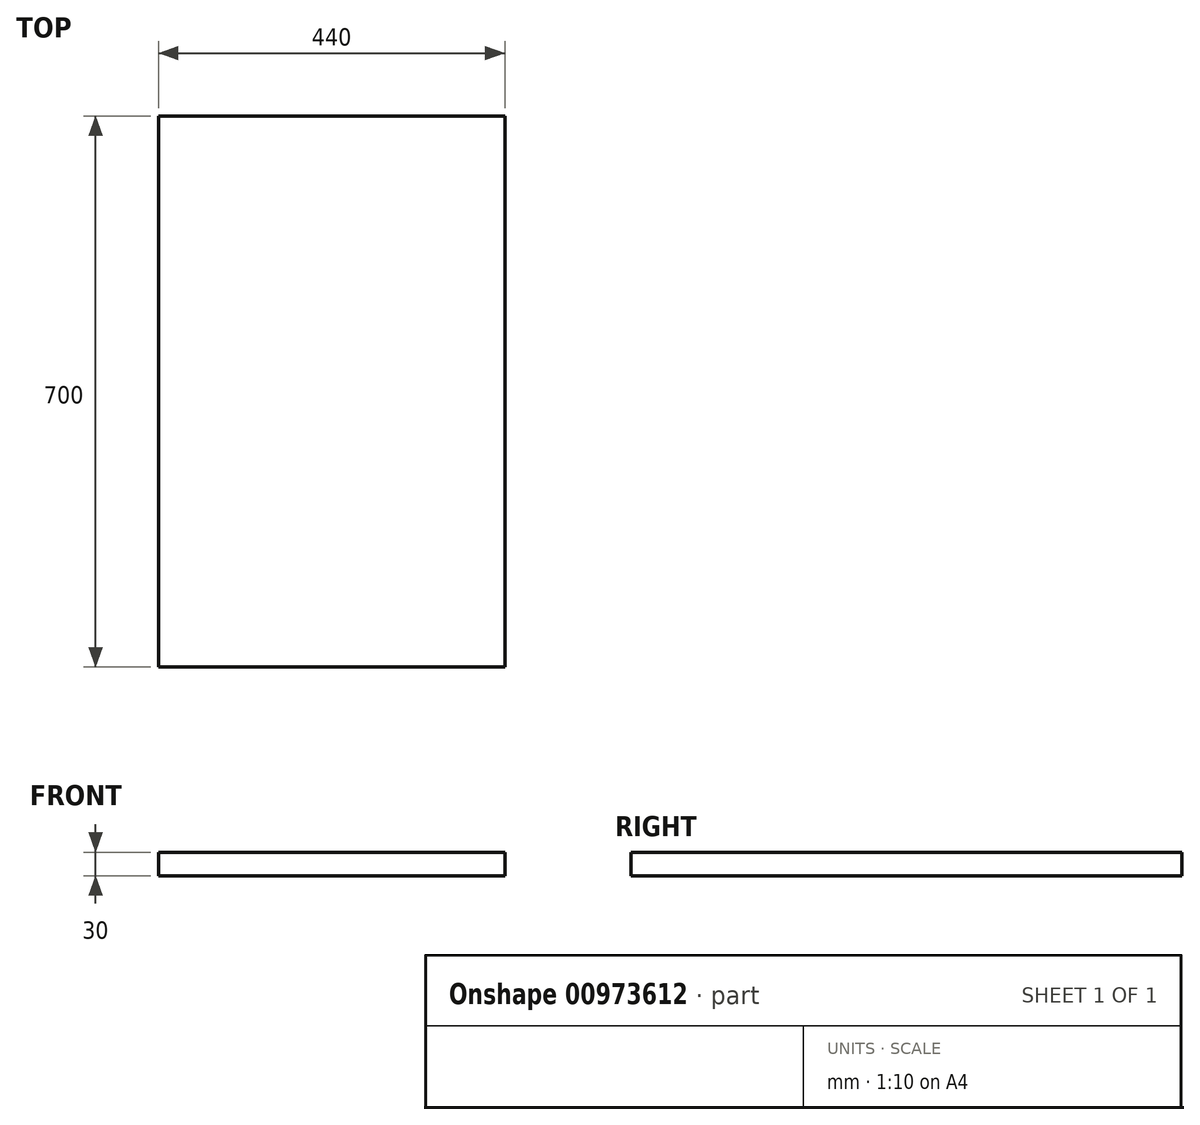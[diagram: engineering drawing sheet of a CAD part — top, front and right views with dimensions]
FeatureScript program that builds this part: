
annotation { "Feature Type Name" : "Feature", "Feature Type Description" : "" }
export const myFeature = defineFeature(function(context is Context, id is Id, definition is map)
    precondition{}
    {
        {
            var Q0;
            Q0=qCreatedBy(makeId("Top.planeOp"),FACE);
            var sketch = newSketch(context, id + "F0", { "sketchPlane" : qUnion([Q0])});
            skLineSegment(sketch, "E0.bottom", {"start": v(220, 350) * mm, "end": v(-220, 350) * mm});
            skLineSegment(sketch, "E0.top", {"start": v(220, -350) * mm, "end": v(-220, -350) * mm});
            skLineSegment(sketch, "E0.left", {"start": v(220, 350) * mm, "end": v(220, -350) * mm});
            skLineSegment(sketch, "E0.right", {"start": v(-220, 350) * mm, "end": v(-220, -350) * mm});
            skPoint(sketch, "E0.middle", {"position": v(0, 0) * mm});
            skSolve(sketch);
        }
        {
            var Q0;
            Q0=makeQuery(id+"F0.imprint","IMPRINT",FACE,{"disambiguationData":[TD([[makeQuery(id+"F0.imprint","IMPRINT",EDGE,{"derivedFrom":sQuery(id+"F0.wireOp",EDGE,"E0.bottom")}),1.0]])]});
            extrude(context, id + "F1", {"entities" : qUnion([Q0]), "depth" : 30 * mm, "offsetDistance" : 25 * mm});
        }
    });
